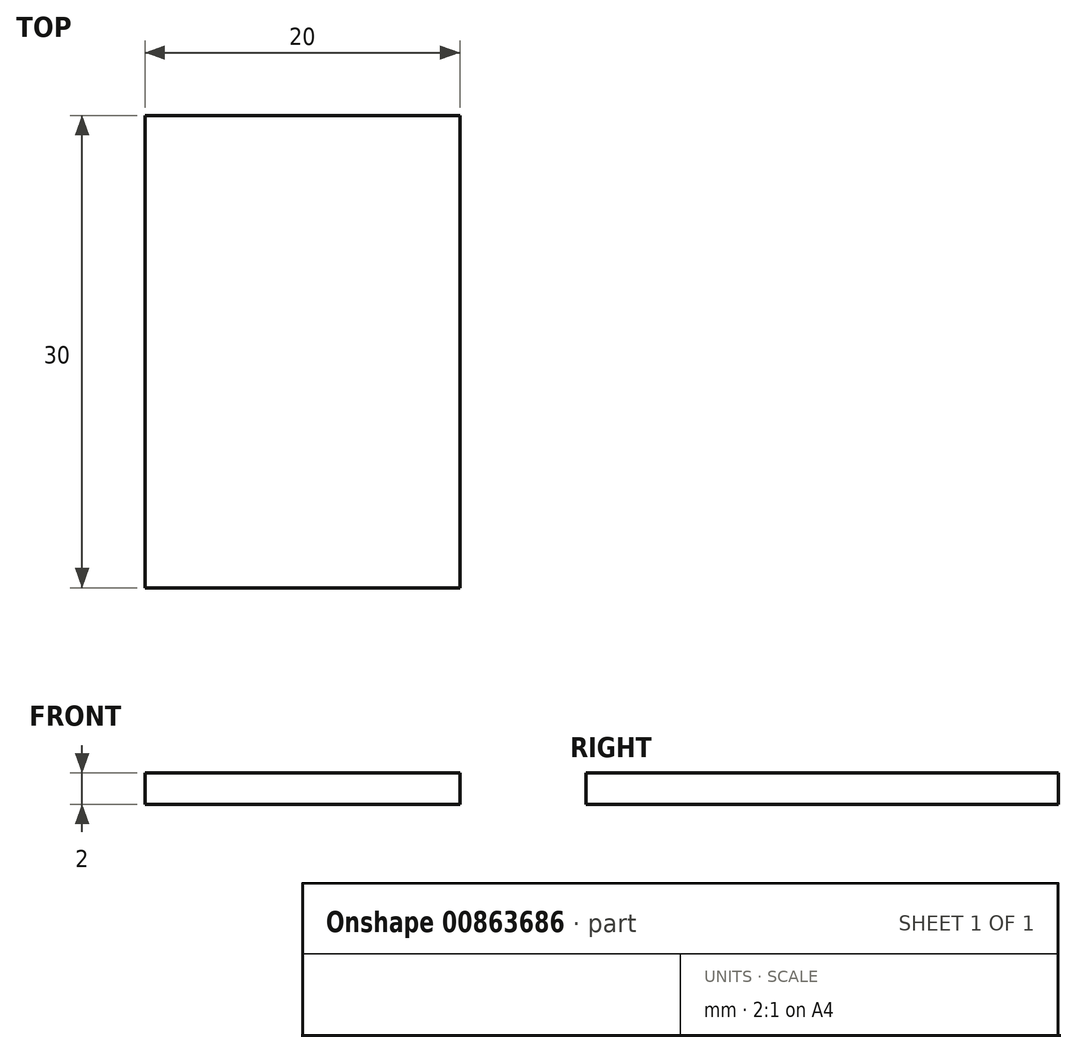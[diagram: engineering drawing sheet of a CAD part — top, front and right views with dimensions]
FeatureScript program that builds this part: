
annotation { "Feature Type Name" : "Feature", "Feature Type Description" : "" }
export const myFeature = defineFeature(function(context is Context, id is Id, definition is map)
    precondition{}
    {
        {
            var Q0;
            Q0=qCreatedBy(makeId("Top.planeOp"),FACE);
            var sketch = newSketch(context, id + "F0", { "sketchPlane" : qUnion([Q0])});
            skLineSegment(sketch, "E0.bottom", {"start": v(0, 0) * mm, "end": v(20, 0) * mm});
            skLineSegment(sketch, "E0.top", {"start": v(0, 30) * mm, "end": v(20, 30) * mm});
            skLineSegment(sketch, "E0.left", {"start": v(0, 0) * mm, "end": v(0, 30) * mm});
            skLineSegment(sketch, "E0.right", {"start": v(20, 0) * mm, "end": v(20, 30) * mm});
            skSolve(sketch);
        }
        {
            var Q0;
            Q0=makeQuery(id+"F0.imprint","IMPRINT",FACE,{"disambiguationData":[TD([[makeQuery(id+"F0.imprint","IMPRINT",EDGE,{"derivedFrom":sQuery(id+"F0.wireOp",EDGE,"E0.bottom")}),1.0]])]});
            extrude(context, id + "F1", {"entities" : qUnion([Q0]), "depth" : 2 * mm, "offsetDistance" : 25 * mm});
        }
    });
